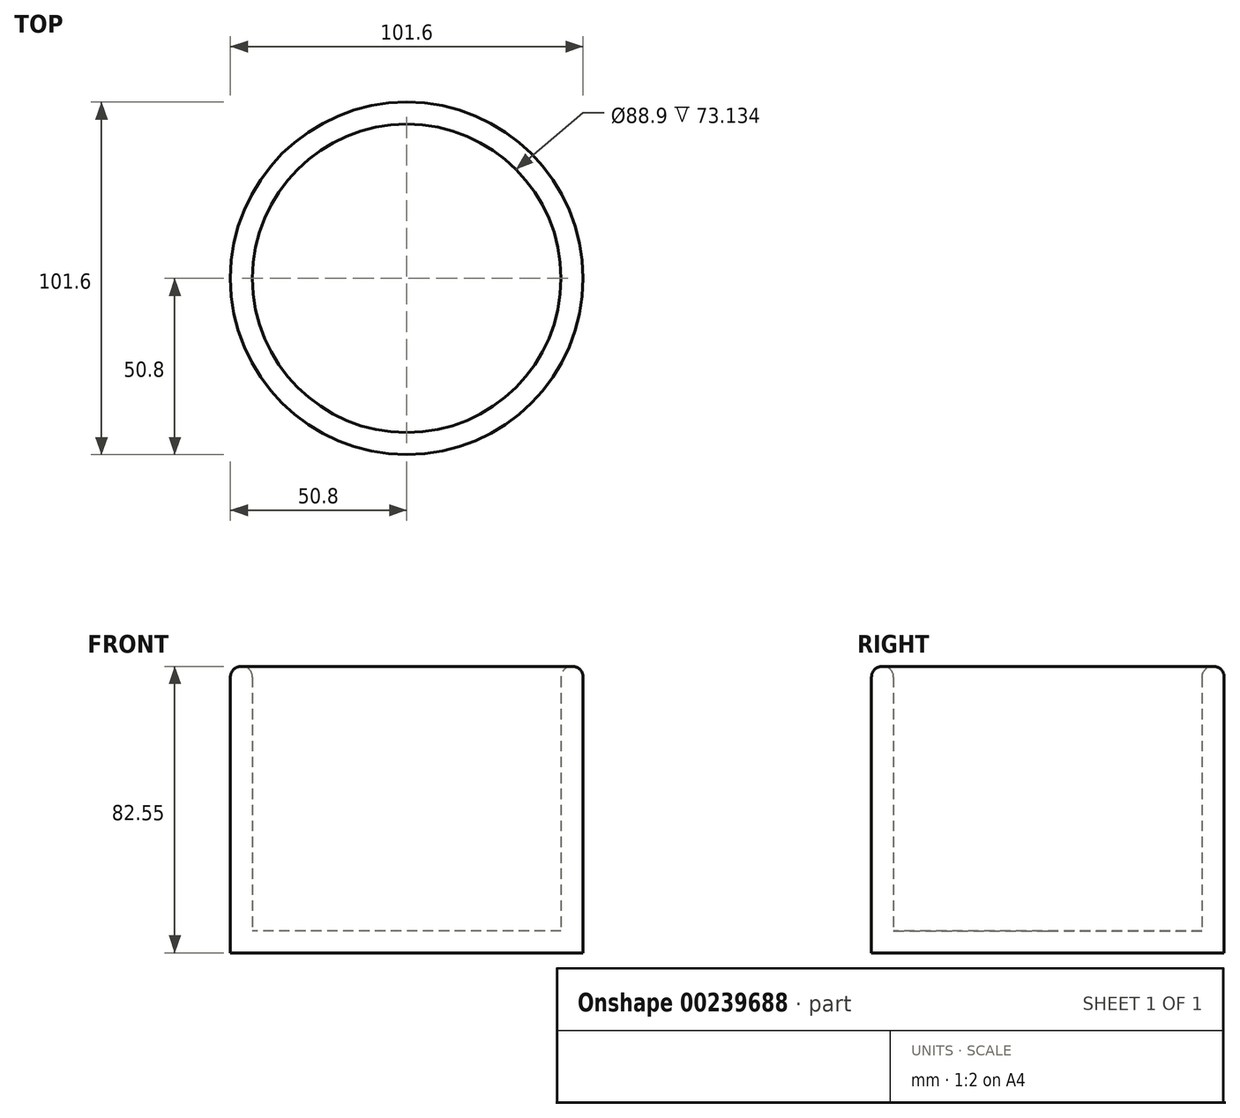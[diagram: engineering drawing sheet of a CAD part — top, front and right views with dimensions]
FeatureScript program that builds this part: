
annotation { "Feature Type Name" : "Feature", "Feature Type Description" : "" }
export const myFeature = defineFeature(function(context is Context, id is Id, definition is map)
    precondition{}
    {
        {
            var Q0;
            Q0=qCreatedBy(makeId("Top.planeOp"),FACE);
            var sketch = newSketch(context, id + "F0", { "sketchPlane" : qUnion([Q0])});
            skCircle(sketch, "E0", {"center": v(0, 0) * mm, "radius": 50.8 * mm});
            skSolve(sketch);
        }
        {
            var Q0;
            Q0=makeQuery(id+"F0.imprint","IMPRINT",FACE,{"disambiguationData":[TD([[makeQuery(id+"F0.imprint","IMPRINT",EDGE,{"derivedFrom":sQuery(id+"F0.wireOp",EDGE,"E0")}),1.0]])]});
            extrude(context, id + "F1", {"entities" : qUnion([Q0]), "oppositeDirection" : true, "depth" : 6.35 * mm});
        }
        {
            var Q0;
            Q0=makeQuery(id+"F1.opExtrude","CAP_FACE",FACE,{"disambiguationData":[OSD([sQuery(id+"F0.wireOp",EDGE,"E0")])],"isStart":true});
            var sketch = newSketch(context, id + "F2", { "sketchPlane" : qUnion([Q0])});
            skCircle(sketch, "E1", {"center": v(0, 0) * mm, "radius": 50.8 * mm});
            skCircle(sketch, "E2", {"center": v(0, 0) * mm, "radius": 44.45 * mm});
            skSolve(sketch);
        }
        {
            var Q0;
            Q0 = qSketchRegion(id + "F2", true);
            extrude(context, id + "F3", {"entities" : qUnion([Q0]), "operationType" : NewBodyOperationType.ADD, "depth" : 76.2 * mm});
        }
        {
            var Q0;
            Q0=makeQuery(id+"F3.opExtrude","CAP_EDGE",EDGE,{"disambiguationData":[OSD([sQuery(id+"F2.wireOp",EDGE,"E1")])],"isStart":false});
            fillet(context, id + "F4", {"entities" : qUnion([Q0]), "radius" : 3.07 * mm, "tangentPropagation" : true, "allowEdgeOverflow" : false});
        }
        {
            var Q0;
            Q0=makeQuery(id+"F3.opExtrude","CAP_EDGE",EDGE,{"disambiguationData":[OSD([sQuery(id+"F2.wireOp",EDGE,"E2")])],"isStart":false});
            fillet(context, id + "F5", {"entities" : qUnion([Q0]), "radius" : 3.07 * mm, "tangentPropagation" : true, "allowEdgeOverflow" : false});
        }
    });
